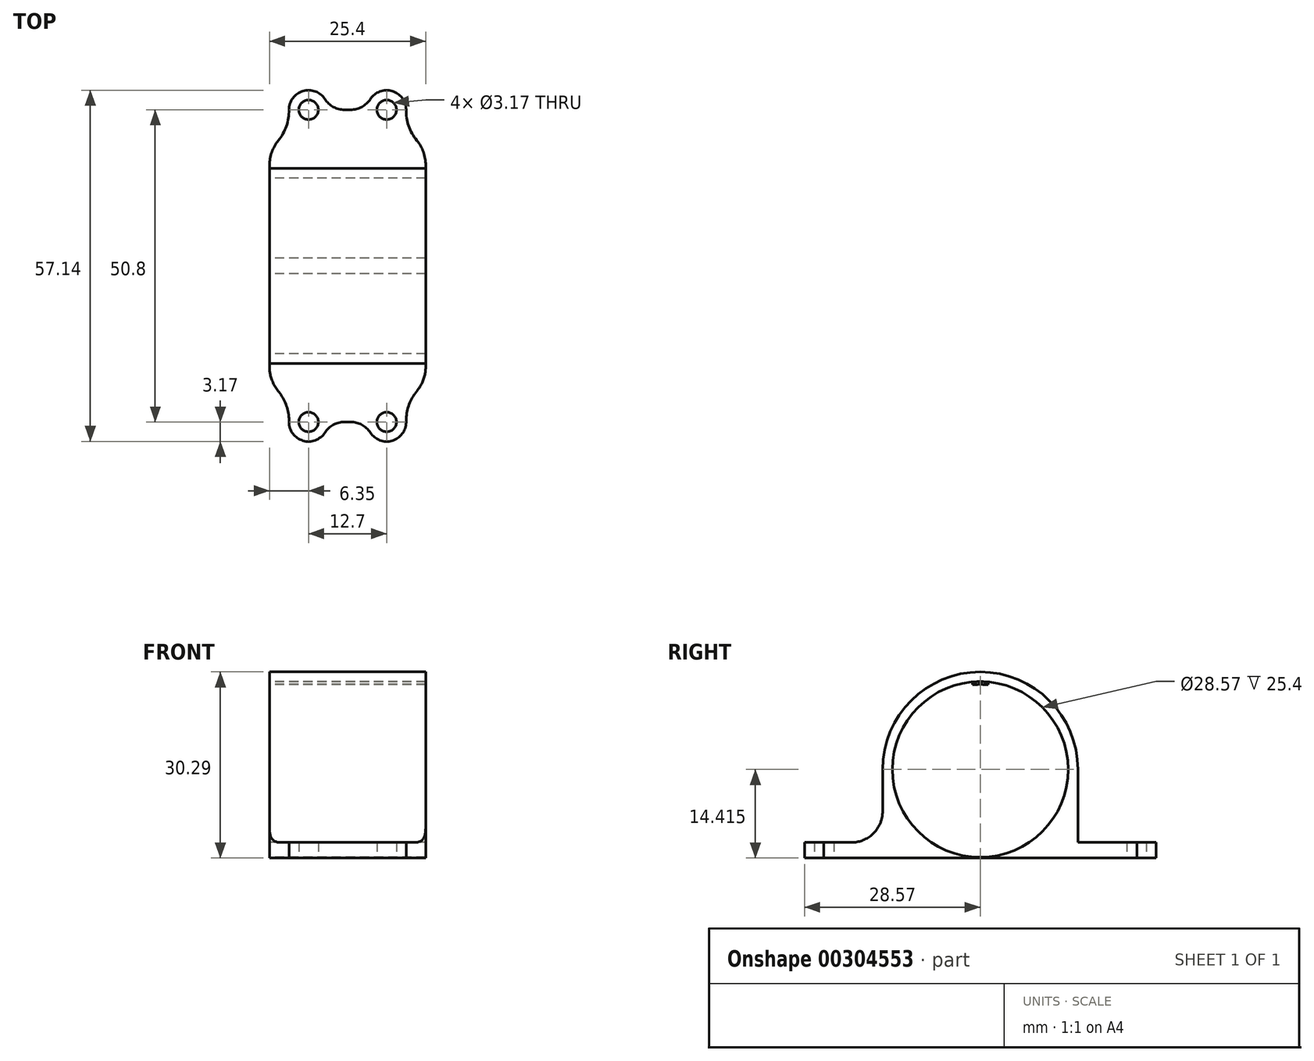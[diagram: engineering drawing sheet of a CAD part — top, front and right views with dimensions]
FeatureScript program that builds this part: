
annotation { "Feature Type Name" : "Feature", "Feature Type Description" : "" }
export const myFeature = defineFeature(function(context is Context, id is Id, definition is map)
    precondition{}
    {
        {
            var Q0;
            Q0=qCreatedBy(makeId("Top.planeOp"),FACE);
            var sketch = newSketch(context, id + "F0", { "sketchPlane" : qUnion([Q0])});
            skLineSegment(sketch, "E0.left", {"start": v(12.7, 0) * mm, "end": v(12.7, -16.37) * mm});
            skLineSegment(sketch, "E0.right", {"start": v(-12.7, 0) * mm, "end": v(-12.7, -16.37) * mm});
            skPoint(sketch, "E0.middle", {"position": v(0, 0) * mm});
            skCircle(sketch, "E1", {"center": v(6.35, -25.4) * mm, "radius": 1.59 * mm});
            skCircle(sketch, "E2", {"center": v(-6.35, -25.4) * mm, "radius": 1.59 * mm});
            skArc(sketch, "E3", {"start": v(-9.52, -25.3) * mm, "mid": v(-7.3, -28.43) * mm, "end": v(-3.69, -27.13) * mm});
            skArc(sketch, "E4", {"start": v(3.69, -27.13) * mm, "mid": v(7.32, -28.42) * mm, "end": v(9.52, -25.25) * mm});
            skArc(sketch, "E5", {"start": v(-9.53, -25.4) * mm, "mid": v(-9.94, -22.75) * mm, "end": v(-11.26, -20.4) * mm});
            skArc(sketch, "E6", {"start": v(11.26, -20.4) * mm, "mid": v(9.93, -22.77) * mm, "end": v(9.52, -25.46) * mm});
            skPoint(sketch, "E7.visualSharp", {"position": v(12.7, -19.05) * mm});
            skArc(sketch, "E7.filletArc", {"start": v(11.26, -20.4) * mm, "mid": v(12.33, -18.51) * mm, "end": v(12.7, -16.37) * mm});
            skPoint(sketch, "E8.visualSharp", {"position": v(-12.7, -19.05) * mm});
            skArc(sketch, "E8.filletArc", {"start": v(-12.7, -16.37) * mm, "mid": v(-12.33, -18.51) * mm, "end": v(-11.26, -20.4) * mm});
            skLineSegment(sketch, "E9.trimOffspring", {"start": v(0.5, -25.4) * mm, "end": v(-0.5, -25.4) * mm});
            skPoint(sketch, "E10.visualSharp", {"position": v(-3.18, -25.4) * mm});
            skArc(sketch, "E10.filletArc", {"start": v(-0.5, -25.4) * mm, "mid": v(-2.31, -25.86) * mm, "end": v(-3.69, -27.13) * mm});
            skPoint(sketch, "E11.visualSharp", {"position": v(3.17, -25.4) * mm});
            skArc(sketch, "E11.filletArc", {"start": v(3.69, -27.13) * mm, "mid": v(2.31, -25.86) * mm, "end": v(0.5, -25.4) * mm});
            skLineSegment(sketch, "E12", {"start": v(0, 0) * mm, "end": v(-12.7, 0) * mm});
            skLineSegment(sketch, "E13", {"start": v(-12.7, 0) * mm, "end": v(12.7, 0) * mm});
            skLineSegment(sketch, "E14.MirrorCS", {"start": v(0.5, 25.4) * mm, "end": v(-0.5, 25.4) * mm});
            skArc(sketch, "E15.MirrorCS", {"start": v(-0.5, 25.4) * mm, "mid": v(-2.31, 25.86) * mm, "end": v(-3.69, 27.13) * mm});
            skArc(sketch, "E16.MirrorCS", {"start": v(-9.53, 25.4) * mm, "mid": v(-9.94, 22.75) * mm, "end": v(-11.26, 20.4) * mm});
            skArc(sketch, "E17.MirrorCS", {"start": v(11.26, 20.4) * mm, "mid": v(9.93, 22.77) * mm, "end": v(9.52, 25.46) * mm});
            skLineSegment(sketch, "E18.MirrorCS", {"start": v(12.7, 0) * mm, "end": v(12.7, 16.37) * mm});
            skCircle(sketch, "E19.MirrorC", {"center": v(6.35, 25.4) * mm, "radius": 1.59 * mm});
            skArc(sketch, "E20.MirrorCS", {"start": v(-9.52, 25.3) * mm, "mid": v(-7.3, 28.43) * mm, "end": v(-3.69, 27.13) * mm});
            skArc(sketch, "E21.MirrorCS", {"start": v(-12.7, 16.37) * mm, "mid": v(-12.33, 18.51) * mm, "end": v(-11.26, 20.4) * mm});
            skLineSegment(sketch, "E22.MirrorCS", {"start": v(-12.7, 0) * mm, "end": v(-12.7, 16.37) * mm});
            skPoint(sketch, "E23.MirrorP", {"position": v(-12.7, 19.05) * mm});
            skCircle(sketch, "E24.MirrorC", {"center": v(-6.35, 25.4) * mm, "radius": 1.59 * mm});
            skArc(sketch, "E25.MirrorCS", {"start": v(3.69, 27.13) * mm, "mid": v(2.31, 25.86) * mm, "end": v(0.5, 25.4) * mm});
            skPoint(sketch, "E26.MirrorP", {"position": v(3.17, 25.4) * mm});
            skPoint(sketch, "E27.MirrorP", {"position": v(-3.18, 25.4) * mm});
            skArc(sketch, "E28.MirrorCS", {"start": v(11.26, 20.4) * mm, "mid": v(12.33, 18.51) * mm, "end": v(12.7, 16.37) * mm});
            skPoint(sketch, "E29.MirrorP", {"position": v(12.7, 19.05) * mm});
            skArc(sketch, "E30.MirrorCS", {"start": v(3.69, 27.13) * mm, "mid": v(7.32, 28.42) * mm, "end": v(9.52, 25.25) * mm});
            skSolve(sketch);
        }
        {
            var Q0;
            Q0=makeQuery(id+"F0.imprint","IMPRINT",FACE,{"disambiguationData":[TD([[makeQuery(id+"F0.imprint","IMPRINT",EDGE,{"derivedFrom":sQuery(id+"F0.wireOp",EDGE,"E13")}),1.0]])]});
            var Q1;
            Q1=makeQuery(id+"F0.imprint","IMPRINT",FACE,{"disambiguationData":[TD([[makeQuery(id+"F0.imprint","IMPRINT",EDGE,{"derivedFrom":sQuery(id+"F0.wireOp",EDGE,"E0.left")}),-1.0]])]});
            extrude(context, id + "F1", {"entities" : qUnion([Q0, Q1]), "depth" : 2.54 * mm});
        }
        {
            var Q0;
            Q0=makeQuery(id+"F1.opExtrude","CAP_FACE",FACE,{"disambiguationData":[OSD([sQuery(id+"F0.wireOp",EDGE,"E0.left"),sQuery(id+"F0.wireOp",EDGE,"E0.right"),sQuery(id+"F0.wireOp",EDGE,"E1"),sQuery(id+"F0.wireOp",EDGE,"E2"),sQuery(id+"F0.wireOp",EDGE,"E3"),sQuery(id+"F0.wireOp",EDGE,"E4"),sQuery(id+"F0.wireOp",EDGE,"E5"),sQuery(id+"F0.wireOp",EDGE,"E6"),sQuery(id+"F0.wireOp",EDGE,"E7.filletArc"),sQuery(id+"F0.wireOp",EDGE,"E8.filletArc"),sQuery(id+"F0.wireOp",EDGE,"E9.trimOffspring"),sQuery(id+"F0.wireOp",EDGE,"E10.filletArc"),sQuery(id+"F0.wireOp",EDGE,"E11.filletArc"),sQuery(id+"F0.wireOp",EDGE,"E14.MirrorCS"),sQuery(id+"F0.wireOp",EDGE,"E15.MirrorCS"),sQuery(id+"F0.wireOp",EDGE,"E16.MirrorCS"),sQuery(id+"F0.wireOp",EDGE,"E17.MirrorCS"),sQuery(id+"F0.wireOp",EDGE,"E18.MirrorCS"),sQuery(id+"F0.wireOp",EDGE,"E19.MirrorC"),sQuery(id+"F0.wireOp",EDGE,"E20.MirrorCS"),sQuery(id+"F0.wireOp",EDGE,"E21.MirrorCS"),sQuery(id+"F0.wireOp",EDGE,"E22.MirrorCS"),sQuery(id+"F0.wireOp",EDGE,"E24.MirrorC"),sQuery(id+"F0.wireOp",EDGE,"E25.MirrorCS"),sQuery(id+"F0.wireOp",EDGE,"E28.MirrorCS"),sQuery(id+"F0.wireOp",EDGE,"E30.MirrorCS")])],"isStart":false});
            var sketch = newSketch(context, id + "F2", { "sketchPlane" : qUnion([Q0])});
            skLineSegment(sketch, "E31.bottom", {"start": v(12.7, 15.88) * mm, "end": v(-12.7, 15.88) * mm});
            skLineSegment(sketch, "E31.top", {"start": v(12.7, -15.88) * mm, "end": v(-12.7, -15.88) * mm});
            skLineSegment(sketch, "E31.left", {"start": v(12.7, 15.88) * mm, "end": v(12.7, -15.88) * mm});
            skLineSegment(sketch, "E31.right", {"start": v(-12.7, 15.88) * mm, "end": v(-12.7, -15.88) * mm});
            skPoint(sketch, "E31.middle", {"position": v(0, 0) * mm});
            skSolve(sketch);
        }
        {
            var Q0;
            Q0=makeQuery(id+"F2.imprint","IMPRINT",FACE,{"disambiguationData":[TD([[makeQuery(id+"F2.imprint","IMPRINT",EDGE,{"derivedFrom":sQuery(id+"F2.wireOp",EDGE,"E31.bottom")}),1.0]])]});
            extrude(context, id + "F3", {"entities" : qUnion([Q0]), "operationType" : NewBodyOperationType.ADD, "depth" : 31.75 * mm});
        }
        {
            var Q0;
            Q0=makeQuery(id+"F3.boolean.opBoolean","MERGE",FACE,{"derivedFrom":[makeQuery(id+"F1.opExtrude","SWEPT_FACE",FACE,{"disambiguationData":[OSD([sQuery(id+"F0.wireOp",EDGE,"E0.right"),sQuery(id+"F0.wireOp",EDGE,"E22.MirrorCS")])]}),makeQuery(id+"F3.opExtrude","SWEPT_FACE",FACE,{"disambiguationData":[OSD([sQuery(id+"F2.wireOp",EDGE,"E31.right")])]})]});
            var sketch = newSketch(context, id + "F4", { "sketchPlane" : qUnion([Q0])});
            skCircle(sketch, "E32", {"center": v(0, 14.41) * mm, "radius": 14.29 * mm});
            skArc(sketch, "E33", {"start": v(15.88, 14.41) * mm, "mid": v(0, 30.29) * mm, "end": v(-15.88, 14.41) * mm});
            skLineSegment(sketch, "E34.left", {"start": v(-15.88, 14.41) * mm, "end": v(-15.88, 2.54) * mm});
            skLineSegment(sketch, "E34.right", {"start": v(15.88, 14.41) * mm, "end": v(15.88, 2.54) * mm});
            skLineSegment(sketch, "E35.top", {"start": v(-15.88, 34.3) * mm, "end": v(15.88, 34.3) * mm});
            skLineSegment(sketch, "E35.left", {"start": v(-15.88, 14.41) * mm, "end": v(-15.88, 34.3) * mm});
            skLineSegment(sketch, "E35.right", {"start": v(15.88, 14.41) * mm, "end": v(15.88, 34.3) * mm});
            skSolve(sketch);
        }
        {
            var Q0;
            Q0=makeQuery(id+"F4.imprint","IMPRINT",FACE,{"disambiguationData":[TD([[makeQuery(id+"F4.imprint","IMPRINT",EDGE,{"derivedFrom":sQuery(id+"F4.wireOp",EDGE,"E33")}),-1.0]])]});
            var Q1;
            Q1=makeQuery(id+"F4.imprint","IMPRINT",FACE,{"disambiguationData":[TD([[makeQuery(id+"F4.imprint","IMPRINT",EDGE,{"derivedFrom":sQuery(id+"F4.wireOp",EDGE,"E32")}),1.0]])]});
            extrude(context, id + "F5", {"entities" : qUnion([Q0, Q1]), "operationType" : NewBodyOperationType.REMOVE, "oppositeDirection" : true, "depth" : 53.37 * mm});
        }
        {
            var Q0;
            Q0=makeQuery(id+"F3.opExtrude","CAP_EDGE",EDGE,{"disambiguationData":[OSD([sQuery(id+"F2.wireOp",EDGE,"E31.top")])],"isStart":true});
            var Q1;
            Q1=makeQuery(id+"F3.opExtrude","CAP_EDGE",EDGE,{"disambiguationData":[OSD([sQuery(id+"F2.wireOp",EDGE,"E31.bottom")])],"isStart":true});
            fillet(context, id + "F6", {"entities" : qUnion([Q0, Q1]), "radius" : 5.08 * mm, "tangentPropagation" : true, "allowEdgeOverflow" : false});
        }
        {
            var Q0;
            Q0=makeQuery(id+"F3.boolean.opBoolean","MERGE",FACE,{"derivedFrom":[makeQuery(id+"F1.opExtrude","SWEPT_FACE",FACE,{"disambiguationData":[OSD([sQuery(id+"F0.wireOp",EDGE,"E0.right"),sQuery(id+"F0.wireOp",EDGE,"E22.MirrorCS")])]}),makeQuery(id+"F3.opExtrude","SWEPT_FACE",FACE,{"disambiguationData":[OSD([sQuery(id+"F2.wireOp",EDGE,"E31.right")])]})]});
            var sketch = newSketch(context, id + "F7", { "sketchPlane" : qUnion([Q0])});
            skLineSegment(sketch, "E36.top", {"start": v(1.27, 29.21) * mm, "end": v(-1.27, 29.21) * mm});
            skLineSegment(sketch, "E36.left", {"start": v(1.27, 28.2) * mm, "end": v(1.27, 29.21) * mm});
            skLineSegment(sketch, "E36.right", {"start": v(-1.27, 28.2) * mm, "end": v(-1.27, 29.21) * mm});
            skPoint(sketch, "E36.middle", {"position": v(0, 28.7) * mm});
            skArc(sketch, "E37", {"start": v(1.27, 28.2) * mm, "mid": v(0, 28.25) * mm, "end": v(-1.27, 28.2) * mm});
            skSolve(sketch);
        }
        {
            var Q0;
            {var subQ0=sQuery(id+"F7.wireOp",EDGE,"E37");Q0=makeQuery(id+"F7.imprint","IMPRINT",FACE,{"disambiguationData":[TD([[makeQuery(id+"F7.imprint","IMPRINT",EDGE,{"derivedFrom":subQ0}),-1.0]])]});}
            extrude(context, id + "F8", {"entities" : qUnion([Q0]), "oppositeDirection" : true, "depth" : 25.4 * mm});
        }
    });
